# Revit family: AFX-Metropolitan-Vanity_
name_source: partatom
category: Lighting Fixtures
units: mm (PartAtom-declared; Revit-internal decimal feet)

## family parameters
Cut with Voids When Loaded = No
Host = Face
Light Source = No
Maintain Annotation Orientation = No
Part Type = Normal
Room Calculation Point = No
Round Connector Dimension = Use Diameter
Shared = No

## types (2) — shared parameters
Apparent Load = 0 VA
Assembly Code = D5020200
Canopy Finish = AFX - Paint Black
Cap Finish = AFX - Plastic Black
Default Elevation = 48"
Depth = 7 3/8"
Diffuser Finish = AFX - Diffuser
Height = 7 7/8"
Keynote = 12500
Manufacturer = AFX Inc
Power Factor = 1
Product Documentation Link = https://www.afxinc.com
Revit Model Built By = https://www.servex-us.com
Support Finish = AFX - Paint Black
Sustainability = https://lamprecycle.org
Type Comments = Metropolitan
URL = https://www.afxinc.com
Voltage = 120 V

## per-type parameters (varying)
| type | Description | Dist Lighting | Qty | Wattage Comments | Width |
| METV38 | LED Vanity - 38"W x 7 3/8"D x 7 7/8"H | 3 15/16" | 4 | 32W | 38" |
| METV30 | LED Vanity - 30"W x 7 3/8"D x 7 7/8"H | 4 1/32" | 3 | 24W | 30" |

note: column(s) folded — value = type name in every type: Model

## geometry (parser evidence)
native form markers: Sweep x5
no freeform markers — native parametric forms only
